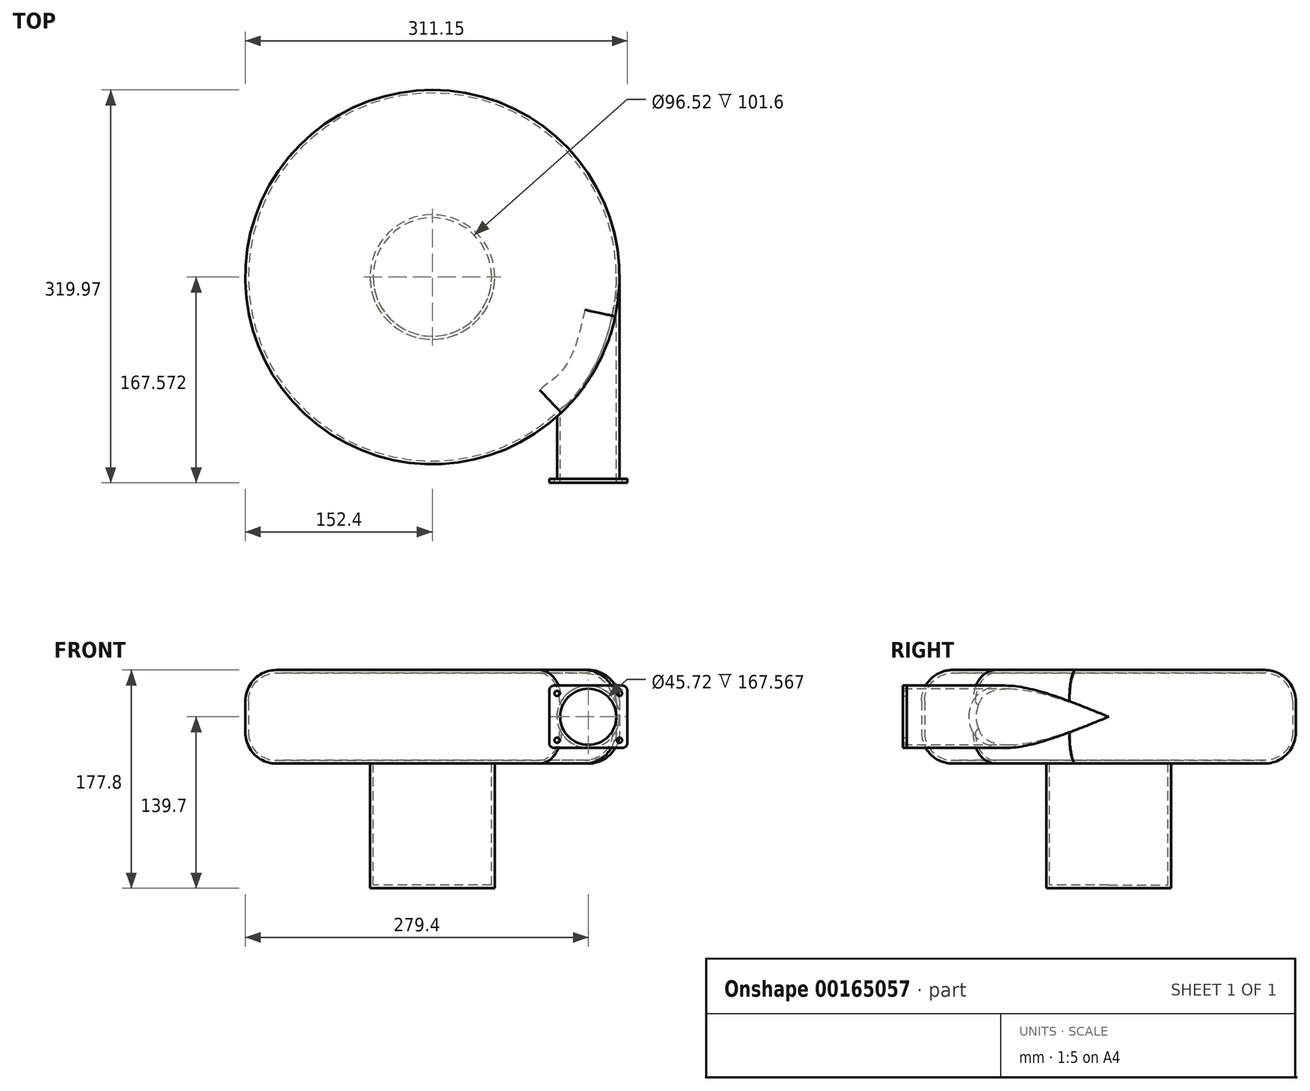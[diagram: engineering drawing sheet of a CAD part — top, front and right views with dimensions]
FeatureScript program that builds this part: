
annotation { "Feature Type Name" : "Feature", "Feature Type Description" : "" }
export const myFeature = defineFeature(function(context is Context, id is Id, definition is map)
    precondition{}
    {
        {
            var Q0;
            Q0=qCreatedBy(makeId("Top.planeOp"),FACE);
            var sketch = newSketch(context, id + "F0", { "sketchPlane" : qUnion([Q0])});
            skLineSegment(sketch, "E0.top", {"start": v(0, -50.8) * mm, "end": v(50.8, -50.8) * mm});
            skLineSegment(sketch, "E0.left", {"start": v(0, 0) * mm, "end": v(0, -50.8) * mm});
            skLineSegment(sketch, "E0.right", {"start": v(50.8, 113.6) * mm, "end": v(50.8, -50.8) * mm});
            skArc(sketch, "E1", {"start": v(50.8, 113.6) * mm, "mid": v(-240.72, 175.8) * mm, "end": v(0, 0) * mm});
            skSolve(sketch);
        }
        {
            var Q0;
            Q0 = qSketchRegion(id + "F0", true);
            extrude(context, id + "F1", {"entities" : qUnion([Q0]), "depth" : 50.8 * mm});
        }
        {
            var Q0;
            Q0=makeQuery(id+"F1.opExtrude","CAP_FACE",FACE,{"disambiguationData":[OSD([sQuery(id+"F0.wireOp",EDGE,"E0.top"),sQuery(id+"F0.wireOp",EDGE,"E0.left"),sQuery(id+"F0.wireOp",EDGE,"E0.right"),sQuery(id+"F0.wireOp",EDGE,"E1")])],"isStart":false});
            var sketch = newSketch(context, id + "F2", { "sketchPlane" : qUnion([Q0])});
            skCircle(sketch, "E2", {"center": v(-101.6, 113.6) * mm, "radius": 152.4 * mm});
            skSolve(sketch);
        }
        {
            var Q0;
            Q0 = qSketchRegion(id + "F2", true);
            extrude(context, id + "F3", {"entities" : qUnion([Q0]), "operationType" : NewBodyOperationType.ADD, "depth" : 12.7 * mm, "hasSecondDirection" : true, "secondDirectionOppositeDirection" : true, "secondDirectionDepth" : 63.5 * mm});
        }
        {
            var Q0;
            Q0=makeQuery(id+"F1.opExtrude","CAP_EDGE",EDGE,{"disambiguationData":[OSD([sQuery(id+"F0.wireOp",EDGE,"E0.left")])],"isStart":false});
            var Q1;
            Q1=makeQuery(id+"F1.opExtrude","CAP_EDGE",EDGE,{"disambiguationData":[OSD([sQuery(id+"F0.wireOp",EDGE,"E0.left")])],"isStart":true});
            var Q2;
            Q2=makeQuery(id+"F1.opExtrude","CAP_EDGE",EDGE,{"disambiguationData":[OSD([sQuery(id+"F0.wireOp",EDGE,"E0.right")])],"isStart":false});
            var Q3;
            Q3=makeQuery(id+"F1.opExtrude","CAP_EDGE",EDGE,{"disambiguationData":[OSD([sQuery(id+"F0.wireOp",EDGE,"E0.right")])],"isStart":true});
            fillet(context, id + "F4", {"entities" : qUnion([Q0, Q1, Q2, Q3]), "radius" : 25.4 * mm, "tangentPropagation" : true, "allowEdgeOverflow" : false});
        }
        {
            var Q0;
            Q0=makeQuery(id+"F3.opExtrude","CAP_EDGE",EDGE,{"disambiguationData":[OSD([sQuery(id+"F2.wireOp",EDGE,"E2")])],"isStart":false});
            var Q1;
            Q1=makeQuery(id+"F3.opExtrude","CAP_EDGE",EDGE,{"disambiguationData":[OSD([sQuery(id+"F2.wireOp",EDGE,"E2")])],"isStart":true});
            fillet(context, id + "F5", {"entities" : qUnion([Q0, Q1]), "radius" : 25.4 * mm, "tangentPropagation" : true, "allowEdgeOverflow" : false});
        }
        {
            var Q0;
            Q0=makeQuery(id+"F3.opExtrude","CAP_FACE",FACE,{"disambiguationData":[OSD([sQuery(id+"F2.wireOp",EDGE,"E2")])],"isStart":true});
            var sketch = newSketch(context, id + "F6", { "sketchPlane" : qUnion([Q0])});
            skCircle(sketch, "E3", {"center": v(-101.6, -113.6) * mm, "radius": 50.8 * mm});
            skSolve(sketch);
        }
        {
            var Q0;
            Q0 = qSketchRegion(id + "F6", true);
            extrude(context, id + "F7", {"entities" : qUnion([Q0]), "operationType" : NewBodyOperationType.ADD, "depth" : 101.6 * mm});
        }
        {
            var Q0;
            Q0=makeQuery(id+"F1.opExtrude","SWEPT_FACE",FACE,{"disambiguationData":[OSD([sQuery(id+"F0.wireOp",EDGE,"E0.top")])]});
            shell(context, id + "F8", {"entities" : qUnion([Q0]), "thickness" : 2.54 * mm});
        }
        {
            var Q0;
            Q0=makeQuery(id+"F1.opExtrude","SWEPT_FACE",FACE,{"disambiguationData":[OSD([sQuery(id+"F0.wireOp",EDGE,"E0.top")])]});
            var sketch = newSketch(context, id + "F9", { "sketchPlane" : qUnion([Q0])});
            skCircle(sketch, "E4", {"center": v(25.4, 25.4) * mm, "radius": 22.86 * mm});
            skLineSegment(sketch, "E5.bottom", {"start": v(57.15, 50.8) * mm, "end": v(-6.35, 50.8) * mm});
            skLineSegment(sketch, "E5.top", {"start": v(57.15, 0) * mm, "end": v(-6.35, 0) * mm});
            skLineSegment(sketch, "E5.left", {"start": v(57.15, 50.8) * mm, "end": v(57.15, 0) * mm});
            skLineSegment(sketch, "E5.right", {"start": v(-6.35, 50.8) * mm, "end": v(-6.35, 0) * mm});
            skLineSegment(sketch, "E6.bottom", {"start": v(50.8, 44.45) * mm, "end": v(0, 44.45) * mm, "construction": true});
            skLineSegment(sketch, "E6.top", {"start": v(50.8, 6.35) * mm, "end": v(0, 6.35) * mm, "construction": true});
            skLineSegment(sketch, "E6.left", {"start": v(50.8, 44.45) * mm, "end": v(50.8, 6.35) * mm, "construction": true});
            skLineSegment(sketch, "E6.right", {"start": v(0, 44.45) * mm, "end": v(0, 6.35) * mm, "construction": true});
            skCircle(sketch, "E7", {"center": v(50.8, 44.45) * mm, "radius": 6.35 * mm, "construction": true});
            skCircle(sketch, "E8", {"center": v(0, 44.45) * mm, "radius": 2.15 * mm});
            skCircle(sketch, "E9", {"center": v(50.8, 44.45) * mm, "radius": 2.15 * mm});
            skCircle(sketch, "E10", {"center": v(50.8, 6.35) * mm, "radius": 2.15 * mm});
            skCircle(sketch, "E11", {"center": v(0, 6.35) * mm, "radius": 2.15 * mm});
            skSolve(sketch);
        }
        {
            var Q0;
            Q0 = qSketchRegion(id + "F9", true);
            extrude(context, id + "F10", {"entities" : qUnion([Q0]), "operationType" : NewBodyOperationType.ADD, "depth" : 3.17 * mm});
        }
        {
            var Q0;
            Q0=makeQuery(id+"F10.opExtrude","SWEPT_EDGE",EDGE,{"disambiguationData":[OSD([sQuery(id+"F9.wireOp",EDGE,"E5.top"),sQuery(id+"F9.wireOp",EDGE,"E5.left")])]});
            var Q1;
            Q1=makeQuery(id+"F10.opExtrude","SWEPT_EDGE",EDGE,{"disambiguationData":[OSD([sQuery(id+"F9.wireOp",EDGE,"E5.top"),sQuery(id+"F9.wireOp",EDGE,"E5.right")])]});
            var Q2;
            Q2=makeQuery(id+"F10.opExtrude","SWEPT_EDGE",EDGE,{"disambiguationData":[OSD([sQuery(id+"F9.wireOp",EDGE,"E5.bottom"),sQuery(id+"F9.wireOp",EDGE,"E5.right")])]});
            var Q3;
            Q3=makeQuery(id+"F10.opExtrude","SWEPT_EDGE",EDGE,{"disambiguationData":[OSD([sQuery(id+"F9.wireOp",EDGE,"E5.bottom"),sQuery(id+"F9.wireOp",EDGE,"E5.left")])]});
            fillet(context, id + "F11", {"entities" : qUnion([Q0, Q1, Q2, Q3]), "radius" : 3.97 * mm, "tangentPropagation" : true, "allowEdgeOverflow" : false});
        }
    });
